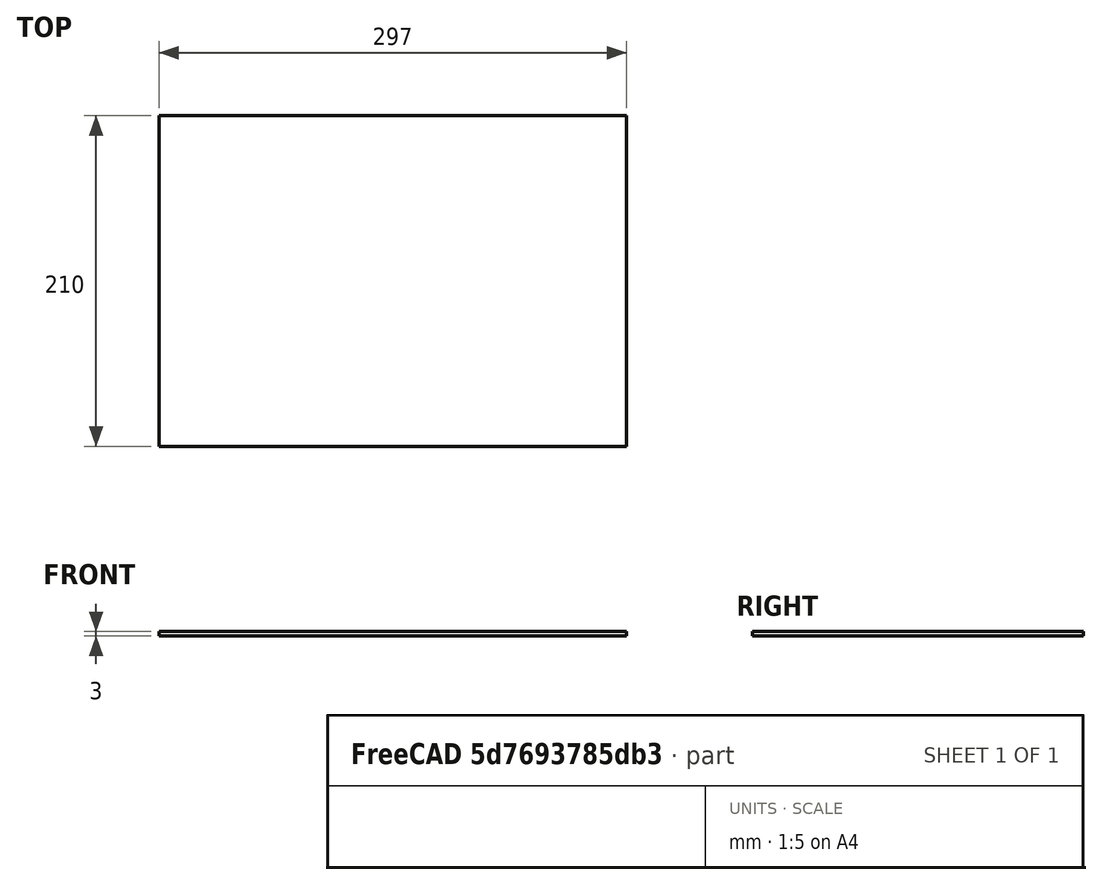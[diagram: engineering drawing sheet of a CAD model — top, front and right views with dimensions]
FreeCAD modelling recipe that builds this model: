
FCSTD DOCUMENT  (FreeCAD 0.20R29177 (Git))
Label: 1001_keyboard_Analog_wood_stencil_A4
License: All rights reserved
LicenseURL: http://en.wikipedia.org/wiki/All_rights_reserved
objects: Sketcher::SketchObject×3, PartDesign::Pad×1, PartDesign::Body×1
note: 6 computed .brp shape members not serialized (recipe doc carries the construction recipe); baked Part::Feature solids carry a one-line shape summary decoded from their .brp

FEATURE [Sketcher::SketchObject] Sketch
  FullyConstrained = true
  MapMode = 5
  Support = -> [XY_Plane]
  sketch-geometry (5):
    g0: LineSegment StartX=0 StartY=210 StartZ=0 EndX=297 EndY=210 EndZ=0
    g1: LineSegment StartX=297 StartY=210 StartZ=0 EndX=297 EndY=0 EndZ=0
    g2: LineSegment StartX=297 StartY=0 StartZ=0 EndX=0 EndY=0 EndZ=0
    g3: LineSegment StartX=0 StartY=0 StartZ=0 EndX=0 EndY=105 EndZ=0
    g4: LineSegment StartX=0 StartY=105 StartZ=0 EndX=0 EndY=210 EndZ=0
  constraints (14):
    c: Coincident(g0,g1)
    c: Coincident(g1,g2)
    c: Horizontal(g0)
    c: Horizontal(g2)
    c: Vertical(g1)
    c: DistanceY(g1,g1) = 210
    c: DistanceX(g0,g0) = 297
    c: Coincident(g3,g2)
    c: Coincident(g4,g0)
    c: Equal(g3,g4)
    c: Vertical(g4)
    c: Vertical(g3)
    c: Coincident(g3,g4)
    c: Coincident(g2,g-1)
FEATURE [PartDesign::Pad] Pad  label="A4_Landscape"
  AllowMultiFace = false
  Direction = (0,0,1)
  Length = 3
  Length2 = 100
  Profile = -> Sketch
  ReferenceAxis = -> Sketch [N_Axis]
  Type = 0
FEATURE [PartDesign::Body] Body
  Group = -> [Sketch,Pad]
  Origin = -> Origin
  Tip = -> Pad
FEATURE [Sketcher::SketchObject] Sketch003  label="JoystickLayout4Way"
  FullyConstrained = false
  sketch-geometry (78):
    g0: LineSegment StartX=34.7688 StartY=185.073 StartZ=0 EndX=129.769 EndY=185.073 EndZ=0
    g1: LineSegment StartX=129.769 StartY=185.073 StartZ=0 EndX=129.769 EndY=130.073 EndZ=0
    g2: LineSegment StartX=129.769 StartY=130.073 StartZ=0 EndX=82.2688 EndY=130.073 EndZ=0
    g3: LineSegment StartX=82.2688 StartY=130.073 StartZ=0 EndX=34.7688 EndY=130.073 EndZ=0
    g4: LineSegment StartX=34.7688 StartY=130.073 StartZ=0 EndX=34.7688 EndY=157.573 EndZ=0
    g5: LineSegment StartX=34.7688 StartY=157.573 StartZ=0 EndX=34.7688 EndY=185.073 EndZ=0
    g6: LineSegment StartX=34.7688 StartY=157.573 StartZ=0 EndX=82.2688 EndY=157.573 EndZ=0
    g7: Circle CenterX=82.2688 CenterY=157.573 CenterZ=0 NormalX=0 NormalY=0 NormalZ=1 AngleXU=0 Radius=15
    g8: LineSegment StartX=82.2688 StartY=157.573 StartZ=0 EndX=129.769 EndY=157.573 EndZ=0
    g9: ArcOfCircle CenterX=40.2688 CenterY=177.573 CenterZ=0 NormalX=0 NormalY=0 NormalZ=1 AngleXU=0 Radius=2.6 StartAngle=1.5708 EndAngle=4.71239
    g10: ArcOfCircle CenterX=42.8688 CenterY=177.573 CenterZ=0 NormalX=0 NormalY=0 NormalZ=1 AngleXU=0 Radius=2.6 StartAngle=4.71239 EndAngle=7.85398
    g11: LineSegment StartX=40.2688 StartY=174.973 StartZ=0 EndX=42.8688 EndY=174.973 EndZ=0
    g12: LineSegment StartX=42.8688 StartY=180.173 StartZ=0 EndX=40.2688 EndY=180.173 EndZ=0
    g13: LineSegment StartX=40.2688 StartY=180.173 StartZ=0 EndX=37.6688 EndY=180.173 EndZ=0
    g14: LineSegment StartX=42.8688 StartY=180.173 StartZ=0 EndX=45.4688 EndY=180.173 EndZ=0
    g15: ArcOfCircle CenterX=124.269 CenterY=177.573 CenterZ=0 NormalX=0 NormalY=0 NormalZ=1 AngleXU=0 Radius=2.6 StartAngle=4.71239 EndAngle=7.85398
    g16: LineSegment StartX=124.269 StartY=180.173 StartZ=0 EndX=121.669 EndY=180.173 EndZ=0
    g17: LineSegment StartX=121.669 StartY=174.973 StartZ=0 EndX=124.269 EndY=174.973 EndZ=0
    g18: ArcOfCircle CenterX=121.669 CenterY=177.573 CenterZ=0 NormalX=0 NormalY=0 NormalZ=1 AngleXU=0 Radius=2.6 StartAngle=1.5708 EndAngle=4.71239
    g19: LineSegment StartX=40.2688 StartY=134.973 StartZ=0 EndX=42.8688 EndY=134.973 EndZ=0
    g20: ArcOfCircle CenterX=42.8688 CenterY=137.573 CenterZ=0 NormalX=0 NormalY=0 NormalZ=1 AngleXU=0 Radius=2.6 StartAngle=4.71239 EndAngle=7.85398
    g21: LineSegment StartX=42.8688 StartY=140.173 StartZ=0 EndX=40.2688 EndY=140.173 EndZ=0
    g22: ArcOfCircle CenterX=40.2688 CenterY=137.573 CenterZ=0 NormalX=0 NormalY=0 NormalZ=1 AngleXU=0 Radius=2.6 StartAngle=1.5708 EndAngle=4.71239
    g23: ArcOfCircle CenterX=121.669 CenterY=137.573 CenterZ=0 NormalX=0 NormalY=0 NormalZ=1 AngleXU=0 Radius=2.6 StartAngle=1.5708 EndAngle=4.71239
    g24: LineSegment StartX=121.669 StartY=134.973 StartZ=0 EndX=124.269 EndY=134.973 EndZ=0
    g25: LineSegment StartX=124.269 StartY=140.173 StartZ=0 EndX=121.669 EndY=140.173 EndZ=0
    g26: ArcOfCircle CenterX=124.269 CenterY=137.573 CenterZ=0 NormalX=0 NormalY=0 NormalZ=1 AngleXU=0 Radius=2.6 StartAngle=4.71239 EndAngle=7.85398
    g27: LineSegment StartX=82.2688 StartY=130.073 StartZ=0 EndX=82.2688 EndY=132.973 EndZ=0
    g28: LineSegment StartX=34.7688 StartY=157.573 StartZ=0 EndX=37.6695 EndY=157.573 EndZ=0
    g29: LineSegment StartX=129.769 StartY=157.573 StartZ=0 EndX=126.868 EndY=157.573 EndZ=0
    g30: LineSegment StartX=82.2688 StartY=185.073 StartZ=0 EndX=82.2688 EndY=182.172 EndZ=0
    g31: LineSegment StartX=129.769 StartY=185.073 StartZ=0 EndX=72.7688 EndY=185.073 EndZ=0
    g32: LineSegment StartX=72.7688 StartY=185.073 StartZ=0 EndX=72.7688 EndY=195.073 EndZ=0
    g33: LineSegment StartX=52.7688 StartY=195.073 StartZ=0 EndX=52.7688 EndY=185.073 EndZ=0
    g34: LineSegment StartX=52.7688 StartY=185.073 StartZ=0 EndX=34.7688 EndY=185.073 EndZ=0
    g35: LineSegment StartX=52.7688 StartY=195.073 StartZ=0 EndX=62.7688 EndY=195.073 EndZ=0
    g36: LineSegment StartX=62.7688 StartY=195.073 StartZ=0 EndX=72.7688 EndY=195.073 EndZ=0
    g37: LineSegment StartX=40.2688 StartY=174.973 StartZ=0 EndX=40.2688 EndY=157.573 EndZ=0
    g38: LineSegment StartX=40.2688 StartY=157.573 StartZ=0 EndX=40.2688 EndY=140.173 EndZ=0
    g39: LineSegment StartX=33.7085 StartY=82.7474 StartZ=0 EndX=128.708 EndY=82.7474 EndZ=0
    g40: LineSegment StartX=128.708 StartY=82.7474 StartZ=0 EndX=128.708 EndY=27.7474 EndZ=0
    g41: LineSegment StartX=128.708 StartY=27.7474 StartZ=0 EndX=81.2085 EndY=27.7474 EndZ=0
    g42: LineSegment StartX=81.2085 StartY=27.7474 StartZ=0 EndX=33.7085 EndY=27.7474 EndZ=0
    g43: LineSegment StartX=33.7085 StartY=27.7474 StartZ=0 EndX=33.7085 EndY=55.2474 EndZ=0
    g44: LineSegment StartX=33.7085 StartY=55.2474 StartZ=0 EndX=33.7085 EndY=82.7474 EndZ=0
    g45: LineSegment StartX=33.7085 StartY=55.2474 StartZ=0 EndX=81.2085 EndY=55.2474 EndZ=0
    g46: Circle CenterX=81.2085 CenterY=55.2474 CenterZ=0 NormalX=0 NormalY=0 NormalZ=1 AngleXU=0 Radius=15
    g47: LineSegment StartX=81.2085 StartY=55.2474 StartZ=0 EndX=128.708 EndY=55.2474 EndZ=0
    g48: ArcOfCircle CenterX=39.2085 CenterY=75.2474 CenterZ=0 NormalX=0 NormalY=0 NormalZ=1 AngleXU=0 Radius=2.6 StartAngle=1.5708 EndAngle=4.71239
    g49: ArcOfCircle CenterX=41.8085 CenterY=75.2474 CenterZ=0 NormalX=0 NormalY=0 NormalZ=1 AngleXU=0 Radius=2.6 StartAngle=4.71239 EndAngle=7.85398
    g50: LineSegment StartX=39.2085 StartY=72.6474 StartZ=0 EndX=41.8085 EndY=72.6474 EndZ=0
    g51: LineSegment StartX=41.8085 StartY=77.8474 StartZ=0 EndX=39.2085 EndY=77.8474 EndZ=0
    g52: LineSegment StartX=39.2085 StartY=77.8474 StartZ=0 EndX=36.6085 EndY=77.8474 EndZ=0
    g53: LineSegment StartX=41.8085 StartY=77.8474 StartZ=0 EndX=44.4085 EndY=77.8474 EndZ=0
    g54: ArcOfCircle CenterX=123.208 CenterY=75.2474 CenterZ=0 NormalX=0 NormalY=0 NormalZ=1 AngleXU=0 Radius=2.6 StartAngle=4.71239 EndAngle=7.85398
    g55: LineSegment StartX=123.208 StartY=77.8474 StartZ=0 EndX=120.608 EndY=77.8474 EndZ=0
    g56: LineSegment StartX=120.608 StartY=72.6474 StartZ=0 EndX=123.208 EndY=72.6474 EndZ=0
    g57: ArcOfCircle CenterX=120.608 CenterY=75.2474 CenterZ=0 NormalX=0 NormalY=0 NormalZ=1 AngleXU=0 Radius=2.6 StartAngle=1.5708 EndAngle=4.71239
    g58: LineSegment StartX=39.2085 StartY=32.6474 StartZ=0 EndX=41.8085 EndY=32.6474 EndZ=0
    g59: ArcOfCircle CenterX=41.8085 CenterY=35.2474 CenterZ=0 NormalX=0 NormalY=0 NormalZ=1 AngleXU=0 Radius=2.6 StartAngle=4.71239 EndAngle=7.85398
    g60: LineSegment StartX=41.8085 StartY=37.8474 StartZ=0 EndX=39.2085 EndY=37.8474 EndZ=0
    g61: ArcOfCircle CenterX=39.2085 CenterY=35.2474 CenterZ=0 NormalX=0 NormalY=0 NormalZ=1 AngleXU=0 Radius=2.6 StartAngle=1.5708 EndAngle=4.71239
    g62: ArcOfCircle CenterX=120.608 CenterY=35.2474 CenterZ=0 NormalX=0 NormalY=0 NormalZ=1 AngleXU=0 Radius=2.6 StartAngle=1.5708 EndAngle=4.71239
    g63: LineSegment StartX=120.608 StartY=32.6474 StartZ=0 EndX=123.208 EndY=32.6474 EndZ=0
    g64: LineSegment StartX=123.208 StartY=37.8474 StartZ=0 EndX=120.608 EndY=37.8474 EndZ=0
    g65: ArcOfCircle CenterX=123.208 CenterY=35.2474 CenterZ=0 NormalX=0 NormalY=0 NormalZ=1 AngleXU=0 Radius=2.6 StartAngle=4.71239 EndAngle=7.85398
    g66: LineSegment StartX=81.2085 StartY=27.7474 StartZ=0 EndX=81.2085 EndY=30.6481 EndZ=0
    g67: LineSegment StartX=33.7085 StartY=55.2474 StartZ=0 EndX=36.6092 EndY=55.2474 EndZ=0
    g68: LineSegment StartX=128.708 StartY=55.2474 StartZ=0 EndX=125.808 EndY=55.2474 EndZ=0
    g69: LineSegment StartX=81.2085 StartY=82.7474 StartZ=0 EndX=81.2085 EndY=79.8467 EndZ=0
    g70: LineSegment StartX=128.708 StartY=82.7474 StartZ=0 EndX=71.7085 EndY=82.7474 EndZ=0
    g71: LineSegment StartX=71.7085 StartY=82.7474 StartZ=0 EndX=71.7085 EndY=92.7474 EndZ=0
    g72: LineSegment StartX=51.7085 StartY=92.7474 StartZ=0 EndX=51.7085 EndY=82.7474 EndZ=0
    g73: LineSegment StartX=51.7085 StartY=82.7474 StartZ=0 EndX=33.7085 EndY=82.7474 EndZ=0
    g74: LineSegment StartX=51.7085 StartY=92.7474 StartZ=0 EndX=61.7085 EndY=92.7474 EndZ=0
    g75: LineSegment StartX=61.7085 StartY=92.7474 StartZ=0 EndX=71.7085 EndY=92.7474 EndZ=0
    g76: LineSegment StartX=39.2085 StartY=72.6474 StartZ=0 EndX=39.2085 EndY=55.2474 EndZ=0
    g77: LineSegment StartX=39.2085 StartY=55.2474 StartZ=0 EndX=39.2085 EndY=37.8474 EndZ=0
  constraints (210):
    c: Coincident(g0,g1)
    c: Coincident(g1,g2)
    c: Horizontal(g0)
    c: Horizontal(g2)
    c: Vertical(g1)
    c: DistanceY(g1,g1) = 55
    c: DistanceX(g0,g0) = 95
    c: Coincident(g3,g2)
    c: Coincident(g4,g3)
    c: Coincident(g5,g4)
    c: Coincident(g5,g0)
    c: Vertical(g5)
    c: Vertical(g4)
    c: Horizontal(g3)
    c: Equal(g3,g2)
    c: Equal(g4,g5)
    c: Coincident(g6,g4)
    c: Horizontal(g6)
    c: Coincident(g7,g6)
    c: Coincident(g8,g6)
    c: PointOnObject(g8,g1)
    c: Horizontal(g8)
    c: Equal(g8,g6)
    c: Diameter(g7) = 30
    c: Tangent(g9,g11) = -1.5708
    c: Tangent(g11,g10) = -1.5708
    c: Tangent(g10,g12) = -1.5708
    c: Tangent(g12,g9) = -1.5708
    c: Equal(g9,g10)
    c: Horizontal(g11)
    c: DistanceY(g10,g10) = 5.2
    c: Coincident(g13,g9)
    c: Horizontal(g13)
    c: Coincident(g14,g10)
    c: Horizontal(g14)
    c: Equal(g14,g13)
    c: DistanceX(g13,g13) = 2.6
    c: DistanceX(g13,g14) = 7.8
    c: Tangent(g18,g17) = -1.5708
    c: Tangent(g17,g15) = -1.5708
    c: Tangent(g15,g16) = -1.5708
    c: Tangent(g16,g18) = -1.5708
    c: Equal(g18,g15)
    c: Horizontal(g17)
    c: Equal(g10,g15) = 5.2
    c: Tangent(g22,g19) = -1.5708
    c: Tangent(g19,g20) = -1.5708
    c: Tangent(g20,g21) = -1.5708
    c: Tangent(g21,g22) = -1.5708
    c: Equal(g22,g20)
    c: Horizontal(g19)
    c: Equal(g10,g20) = 5.2
    c: Tangent(g23,g24) = -1.5708
    c: Tangent(g24,g26) = -1.5708
    c: Tangent(g26,g25) = -1.5708
    c: Tangent(g25,g23) = -1.5708
    c: Equal(g23,g26)
    c: Horizontal(g24)
    c: Equal(g10,g26) = 5.2
    c: Equal(g21,g16)
    c: Equal(g16,g25)
    c: Equal(g25,g11)
    c: Vertical(g21,g9)
    c: DistanceX(g9,g6) = 42
    c: Horizontal(g23,g20)
    c: Vertical(g23,g17)
    c: DistanceX(g9,g15) = 84
    c: Horizontal(g10,g16)
    c: Coincident(g27,g2)
    c: Vertical(g27)
    c: Coincident(g28,g4)
    c: PointOnObject(g28,g6)
    c: Equal(g28,g27)
    c: Coincident(g29,g8)
    c: PointOnObject(g29,g8)
    c: Equal(g29,g27)
    c: PointOnObject(g30,g0)
    c: Vertical(g30)
    c: Equal(g30,g29)
    c: Vertical(g30,g27)
    c: Coincident(g31,g1)
    c: PointOnObject(g31,g0)
    c: Coincident(g32,g31)
    c: Vertical(g32)
    c: PointOnObject(g33,g0)
    c: Vertical(g33)
    c: Coincident(g34,g33)
    c: Coincident(g34,g5)
    c: DistanceX(g33,g32) = 20
    c: DistanceY(g33,g33) = 10
    c: Coincident(g35,g33)
    c: Horizontal(g35)
    c: Coincident(g36,g35)
    c: Coincident(g36,g32)
    c: Horizontal(g36)
    c: Equal(g36,g35)
    c: DistanceX(g5,g35) = 28
    c: Coincident(g37,g9)
    c: PointOnObject(g37,g6)
    c: Vertical(g37)
    c: Coincident(g38,g37)
    c: Coincident(g38,g21)
    c: Equal(g38,g37)
    c: DistanceY(g22,g9) = 40
    c: DistanceX(g7,g15) = 42
    c: Coincident(g39,g40)
    c: Coincident(g40,g41)
    c: Horizontal(g39)
    c: Horizontal(g41)
    c: Vertical(g40)
    c: DistanceY(g40,g40) = 55
    c: DistanceX(g39,g39) = 95
    c: Coincident(g42,g41)
    c: Coincident(g43,g42)
    c: Coincident(g44,g43)
    c: Coincident(g44,g39)
    c: Vertical(g44)
    c: Vertical(g43)
    c: Horizontal(g42)
    c: Equal(g42,g41)
    c: Equal(g43,g44)
    c: Coincident(g45,g43)
    c: Horizontal(g45)
    c: Coincident(g46,g45)
    c: Coincident(g47,g45)
    c: PointOnObject(g47,g40)
    c: Horizontal(g47)
    c: Equal(g47,g45)
    c: Diameter(g46) = 30
    c: Tangent(g48,g50) = -1.5708
    c: Tangent(g50,g49) = -1.5708
    c: Tangent(g49,g51) = -1.5708
    c: Tangent(g51,g48) = -1.5708
    c: Equal(g48,g49)
    c: Horizontal(g50)
    c: DistanceY(g49,g49) = 5.2
    c: Coincident(g52,g48)
    c: Horizontal(g52)
    c: Coincident(g53,g49)
    c: Horizontal(g53)
    c: Equal(g53,g52)
    c: DistanceX(g52,g52) = 2.6
    c: DistanceX(g52,g53) = 7.8
    c: Tangent(g57,g56) = -1.5708
    c: Tangent(g56,g54) = -1.5708
    c: Tangent(g54,g55) = -1.5708
    c: Tangent(g55,g57) = -1.5708
    c: Equal(g57,g54)
    c: Horizontal(g56)
    c: Equal(g49,g54) = 5.2
    c: Tangent(g61,g58) = -1.5708
    c: Tangent(g58,g59) = -1.5708
    c: Tangent(g59,g60) = -1.5708
    c: Tangent(g60,g61) = -1.5708
    c: Equal(g61,g59)
    c: Horizontal(g58)
    c: Equal(g49,g59) = 5.2
    c: Tangent(g62,g63) = -1.5708
    c: Tangent(g63,g65) = -1.5708
    c: Tangent(g65,g64) = -1.5708
    c: Tangent(g64,g62) = -1.5708
    c: Equal(g62,g65)
    c: Horizontal(g63)
    c: Equal(g49,g65) = 5.2
    c: Equal(g60,g55)
    c: Equal(g55,g64)
    c: Equal(g64,g50)
    c: Vertical(g60,g48)
    c: DistanceX(g48,g45) = 42
    c: Horizontal(g62,g59)
    c: Vertical(g62,g56)
    c: DistanceX(g48,g54) = 84
    c: Horizontal(g49,g55)
    c: Coincident(g66,g41)
    c: Vertical(g66)
    c: Coincident(g67,g43)
    c: PointOnObject(g67,g45)
    c: Equal(g67,g66)
    c: Coincident(g68,g47)
    c: PointOnObject(g68,g47)
    c: Equal(g68,g66)
    c: PointOnObject(g69,g39)
    c: Vertical(g69)
    c: Equal(g69,g68)
    c: Vertical(g69,g66)
    c: Coincident(g70,g40)
    c: PointOnObject(g70,g39)
    c: Coincident(g71,g70)
    c: Vertical(g71)
    c: PointOnObject(g72,g39)
    c: Vertical(g72)
    c: Coincident(g73,g72)
    c: Coincident(g73,g44)
    c: DistanceX(g72,g71) = 20
    c: DistanceY(g72,g72) = 10
    c: Coincident(g74,g72)
    c: Horizontal(g74)
    c: Coincident(g75,g74)
    c: Coincident(g75,g71)
    c: Horizontal(g75)
    c: Equal(g75,g74)
    c: DistanceX(g44,g74) = 28
    c: Coincident(g76,g48)
    c: PointOnObject(g76,g45)
    c: Vertical(g76)
    c: Coincident(g77,g76)
    c: Coincident(g77,g60)
    c: Equal(g77,g76)
    c: DistanceY(g61,g48) = 40
    c: DistanceX(g46,g54) = 42
FEATURE [Sketcher::SketchObject] Sketch007  label="JoystickAnalog"
  FullyConstrained = false
  MapMode = 5
  Support = -> [XY_Plane]
  sketch-geometry (90):
    g0: Circle CenterX=230.411 CenterY=57.5212 CenterZ=0 NormalX=0 NormalY=0 NormalZ=1 AngleXU=0 Radius=20
    g1: LineSegment StartX=230.411 StartY=57.5212 StartZ=0 EndX=187.911 EndY=57.5212 EndZ=0
    g2: LineSegment StartX=230.411 StartY=57.5212 StartZ=0 EndX=272.911 EndY=57.5212 EndZ=0
    g3: LineSegment StartX=187.911 StartY=57.5212 StartZ=0 EndX=187.911 EndY=77.5212 EndZ=0
    g4: LineSegment StartX=187.911 StartY=57.5212 StartZ=0 EndX=187.911 EndY=37.5212 EndZ=0
    g5: LineSegment StartX=272.911 StartY=57.5212 StartZ=0 EndX=272.911 EndY=37.5212 EndZ=0
    g6: LineSegment StartX=272.911 StartY=57.5212 StartZ=0 EndX=272.911 EndY=77.5212 EndZ=0
    g7: LineSegment StartX=230.411 StartY=57.5212 StartZ=0 EndX=230.411 EndY=87.5212 EndZ=0
    g8: LineSegment StartX=230.411 StartY=57.5212 StartZ=0 EndX=230.411 EndY=27.5212 EndZ=0
    g9: LineSegment StartX=230.411 StartY=87.5212 StartZ=0 EndX=182.911 EndY=87.5212 EndZ=0
    g10: LineSegment StartX=230.411 StartY=87.5212 StartZ=0 EndX=277.911 EndY=87.5212 EndZ=0
    g11: LineSegment StartX=230.411 StartY=27.5212 StartZ=0 EndX=182.911 EndY=27.5212 EndZ=0
    g12: LineSegment StartX=182.911 StartY=27.5212 StartZ=0 EndX=182.911 EndY=87.5212 EndZ=0
    g13: LineSegment StartX=230.411 StartY=27.5212 StartZ=0 EndX=277.911 EndY=27.5212 EndZ=0
    g14: LineSegment StartX=277.911 StartY=27.5212 StartZ=0 EndX=277.911 EndY=87.5212 EndZ=0
    g15: ArcOfCircle CenterX=187.911 CenterY=77.5212 CenterZ=0 NormalX=0 NormalY=0 NormalZ=1 AngleXU=0 Radius=2.5 StartAngle=1.5708 EndAngle=4.71239
    g16: ArcOfCircle CenterX=192.911 CenterY=77.5212 CenterZ=0 NormalX=0 NormalY=0 NormalZ=1 AngleXU=0 Radius=2.5 StartAngle=4.71239 EndAngle=7.85398
    g17: LineSegment StartX=187.911 StartY=75.0212 StartZ=0 EndX=192.911 EndY=75.0212 EndZ=0
    g18: LineSegment StartX=192.911 StartY=80.0212 StartZ=0 EndX=187.911 EndY=80.0212 EndZ=0
    g19: ArcOfCircle CenterX=187.911 CenterY=37.5212 CenterZ=0 NormalX=0 NormalY=0 NormalZ=1 AngleXU=0 Radius=2.5 StartAngle=1.5708 EndAngle=4.71239
    g20: ArcOfCircle CenterX=192.911 CenterY=37.5212 CenterZ=0 NormalX=0 NormalY=0 NormalZ=1 AngleXU=0 Radius=2.5 StartAngle=4.71239 EndAngle=7.85398
    g21: LineSegment StartX=187.911 StartY=35.0212 StartZ=0 EndX=192.911 EndY=35.0212 EndZ=0
    g22: LineSegment StartX=192.911 StartY=40.0212 StartZ=0 EndX=187.911 EndY=40.0212 EndZ=0
    g23: ArcOfCircle CenterX=272.911 CenterY=37.5212 CenterZ=0 NormalX=0 NormalY=0 NormalZ=1 AngleXU=0 Radius=2.5 StartAngle=4.71239 EndAngle=7.85398
    g24: ArcOfCircle CenterX=267.911 CenterY=37.5212 CenterZ=0 NormalX=0 NormalY=0 NormalZ=1 AngleXU=0 Radius=2.5 StartAngle=1.5708 EndAngle=4.71239
    g25: LineSegment StartX=272.911 StartY=40.0212 StartZ=0 EndX=267.911 EndY=40.0212 EndZ=0
    g26: LineSegment StartX=267.911 StartY=35.0212 StartZ=0 EndX=272.911 EndY=35.0212 EndZ=0
    g27: ArcOfCircle CenterX=272.911 CenterY=77.5212 CenterZ=0 NormalX=0 NormalY=0 NormalZ=1 AngleXU=0 Radius=2.5 StartAngle=4.71239 EndAngle=7.85398
    g28: ArcOfCircle CenterX=267.911 CenterY=77.5212 CenterZ=0 NormalX=0 NormalY=0 NormalZ=1 AngleXU=0 Radius=2.5 StartAngle=1.5708 EndAngle=4.71239
    g29: LineSegment StartX=272.911 StartY=80.0212 StartZ=0 EndX=267.911 EndY=80.0212 EndZ=0
    g30: LineSegment StartX=267.911 StartY=75.0212 StartZ=0 EndX=272.911 EndY=75.0212 EndZ=0
    g31: LineSegment StartX=187.911 StartY=57.5212 StartZ=0 EndX=182.911 EndY=57.5212 EndZ=0
    g32: LineSegment StartX=272.911 StartY=57.5212 StartZ=0 EndX=277.911 EndY=57.5212 EndZ=0
    g33: LineSegment StartX=230.411 StartY=87.5212 StartZ=0 EndX=230.411 EndY=82.5212 EndZ=0
    g34: LineSegment StartX=182.911 StartY=27.5212 StartZ=0 EndX=222.911 EndY=27.5212 EndZ=0
    g35: LineSegment StartX=222.911 StartY=27.5212 StartZ=0 EndX=222.911 EndY=15.5212 EndZ=0
    g36: LineSegment StartX=222.911 StartY=15.5212 StartZ=0 EndX=237.911 EndY=15.5212 EndZ=0
    g37: LineSegment StartX=237.911 StartY=15.5212 StartZ=0 EndX=237.911 EndY=27.5212 EndZ=0
    g38: LineSegment StartX=237.911 StartY=27.5212 StartZ=0 EndX=277.911 EndY=27.5212 EndZ=0
    g39: LineSegment StartX=182.911 StartY=87.5212 StartZ=0 EndX=215.411 EndY=87.5212 EndZ=0
    g40: LineSegment StartX=215.411 StartY=87.5212 StartZ=0 EndX=215.411 EndY=91.5212 EndZ=0
    g41: LineSegment StartX=220.411 StartY=91.5212 StartZ=0 EndX=220.411 EndY=87.5212 EndZ=0
    g42: LineSegment StartX=220.411 StartY=87.5212 StartZ=0 EndX=230.411 EndY=87.5212 EndZ=0
    g43: LineSegment StartX=215.411 StartY=91.5212 StartZ=0 EndX=217.911 EndY=91.5212 EndZ=0
    g44: LineSegment StartX=217.911 StartY=91.5212 StartZ=0 EndX=220.411 EndY=91.5212 EndZ=0
    g45: Circle CenterX=228.24 CenterY=157.793 CenterZ=0 NormalX=0 NormalY=0 NormalZ=1 AngleXU=0 Radius=20
    g46: LineSegment StartX=228.24 StartY=157.793 StartZ=0 EndX=185.74 EndY=157.793 EndZ=0
    g47: LineSegment StartX=228.24 StartY=157.793 StartZ=0 EndX=270.74 EndY=157.793 EndZ=0
    g48: LineSegment StartX=185.74 StartY=157.793 StartZ=0 EndX=185.74 EndY=177.793 EndZ=0
    g49: LineSegment StartX=185.74 StartY=157.793 StartZ=0 EndX=185.74 EndY=137.793 EndZ=0
    g50: LineSegment StartX=270.74 StartY=157.793 StartZ=0 EndX=270.74 EndY=137.793 EndZ=0
    g51: LineSegment StartX=270.74 StartY=157.793 StartZ=0 EndX=270.74 EndY=177.793 EndZ=0
    g52: LineSegment StartX=228.24 StartY=157.793 StartZ=0 EndX=228.24 EndY=187.793 EndZ=0
    g53: LineSegment StartX=228.24 StartY=157.793 StartZ=0 EndX=228.24 EndY=127.793 EndZ=0
    g54: LineSegment StartX=228.24 StartY=187.793 StartZ=0 EndX=180.74 EndY=187.793 EndZ=0
    g55: LineSegment StartX=228.24 StartY=187.793 StartZ=0 EndX=275.74 EndY=187.793 EndZ=0
    g56: LineSegment StartX=228.24 StartY=127.793 StartZ=0 EndX=180.74 EndY=127.793 EndZ=0
    g57: LineSegment StartX=180.74 StartY=127.793 StartZ=0 EndX=180.74 EndY=187.793 EndZ=0
    g58: LineSegment StartX=228.24 StartY=127.793 StartZ=0 EndX=275.74 EndY=127.793 EndZ=0
    g59: LineSegment StartX=275.74 StartY=127.793 StartZ=0 EndX=275.74 EndY=187.793 EndZ=0
    g60: ArcOfCircle CenterX=185.74 CenterY=177.793 CenterZ=0 NormalX=0 NormalY=0 NormalZ=1 AngleXU=0 Radius=2.5 StartAngle=1.5708 EndAngle=4.71239
    g61: ArcOfCircle CenterX=190.74 CenterY=177.793 CenterZ=0 NormalX=0 NormalY=0 NormalZ=1 AngleXU=0 Radius=2.5 StartAngle=4.71239 EndAngle=7.85398
    g62: LineSegment StartX=185.74 StartY=175.293 StartZ=0 EndX=190.74 EndY=175.293 EndZ=0
    g63: LineSegment StartX=190.74 StartY=180.293 StartZ=0 EndX=185.74 EndY=180.293 EndZ=0
    g64: ArcOfCircle CenterX=185.74 CenterY=137.793 CenterZ=0 NormalX=0 NormalY=0 NormalZ=1 AngleXU=0 Radius=2.5 StartAngle=1.5708 EndAngle=4.71239
    g65: ArcOfCircle CenterX=190.74 CenterY=137.793 CenterZ=0 NormalX=0 NormalY=0 NormalZ=1 AngleXU=0 Radius=2.5 StartAngle=4.71239 EndAngle=7.85398
    g66: LineSegment StartX=185.74 StartY=135.293 StartZ=0 EndX=190.74 EndY=135.293 EndZ=0
    g67: LineSegment StartX=190.74 StartY=140.293 StartZ=0 EndX=185.74 EndY=140.293 EndZ=0
    g68: ArcOfCircle CenterX=270.74 CenterY=137.793 CenterZ=0 NormalX=0 NormalY=0 NormalZ=1 AngleXU=0 Radius=2.5 StartAngle=4.71239 EndAngle=7.85398
    g69: ArcOfCircle CenterX=265.74 CenterY=137.793 CenterZ=0 NormalX=0 NormalY=0 NormalZ=1 AngleXU=0 Radius=2.5 StartAngle=1.5708 EndAngle=4.71239
    g70: LineSegment StartX=270.74 StartY=140.293 StartZ=0 EndX=265.74 EndY=140.293 EndZ=0
    g71: LineSegment StartX=265.74 StartY=135.293 StartZ=0 EndX=270.74 EndY=135.293 EndZ=0
    g72: ArcOfCircle CenterX=270.74 CenterY=177.793 CenterZ=0 NormalX=0 NormalY=0 NormalZ=1 AngleXU=0 Radius=2.5 StartAngle=4.71239 EndAngle=7.85398
    g73: ArcOfCircle CenterX=265.74 CenterY=177.793 CenterZ=0 NormalX=0 NormalY=0 NormalZ=1 AngleXU=0 Radius=2.5 StartAngle=1.5708 EndAngle=4.71239
    g74: LineSegment StartX=270.74 StartY=180.293 StartZ=0 EndX=265.74 EndY=180.293 EndZ=0
    g75: LineSegment StartX=265.74 StartY=175.293 StartZ=0 EndX=270.74 EndY=175.293 EndZ=0
    g76: LineSegment StartX=185.74 StartY=157.793 StartZ=0 EndX=180.74 EndY=157.793 EndZ=0
    g77: LineSegment StartX=270.74 StartY=157.793 StartZ=0 EndX=275.74 EndY=157.793 EndZ=0
    g78: LineSegment StartX=228.24 StartY=187.793 StartZ=0 EndX=228.24 EndY=182.793 EndZ=0
    g79: LineSegment StartX=180.74 StartY=127.793 StartZ=0 EndX=220.74 EndY=127.793 EndZ=0
    g80: LineSegment StartX=220.74 StartY=127.793 StartZ=0 EndX=220.74 EndY=115.793 EndZ=0
    g81: LineSegment StartX=220.74 StartY=115.793 StartZ=0 EndX=235.74 EndY=115.793 EndZ=0
    g82: LineSegment StartX=235.74 StartY=115.793 StartZ=0 EndX=235.74 EndY=127.793 EndZ=0
    g83: LineSegment StartX=235.74 StartY=127.793 StartZ=0 EndX=275.74 EndY=127.793 EndZ=0
    g84: LineSegment StartX=180.74 StartY=187.793 StartZ=0 EndX=213.24 EndY=187.793 EndZ=0
    g85: LineSegment StartX=213.24 StartY=187.793 StartZ=0 EndX=213.24 EndY=191.793 EndZ=0
    g86: LineSegment StartX=218.24 StartY=191.793 StartZ=0 EndX=218.24 EndY=187.793 EndZ=0
    g87: LineSegment StartX=218.24 StartY=187.793 StartZ=0 EndX=228.24 EndY=187.793 EndZ=0
    g88: LineSegment StartX=213.24 StartY=191.793 StartZ=0 EndX=215.74 EndY=191.793 EndZ=0
    g89: LineSegment StartX=215.74 StartY=191.793 StartZ=0 EndX=218.24 EndY=191.793 EndZ=0
  constraints (234):
    c: Diameter(g0) = 40
    c: Coincident(g1,g0)
    c: Horizontal(g1)
    c: Coincident(g2,g0)
    c: Horizontal(g2)
    c: Coincident(g3,g1)
    c: Vertical(g3)
    c: Coincident(g4,g1)
    c: Vertical(g4)
    c: Coincident(g5,g2)
    c: Vertical(g5)
    c: Coincident(g6,g2)
    c: Vertical(g6)
    c: Equal(g4,g3)
    c: Equal(g3,g5)
    c: Equal(g5,g6)
    c: Equal(g2,g1)
    c: Coincident(g7,g0)
    c: Vertical(g7)
    c: Coincident(g8,g0)
    c: Vertical(g8)
    c: Equal(g8,g7)
    c: DistanceY(g4,g3) = 40
    c: DistanceX(g3,g6) = 85
    c: DistanceY(g8,g7) = 60
    c: Coincident(g9,g7)
    c: Coincident(g10,g9)
    c: Equal(g10,g9)
    c: Horizontal(g9)
    c: Horizontal(g10)
    c: DistanceX(g9,g10) = 95
    c: Coincident(g11,g8)
    c: Horizontal(g11)
    c: Coincident(g12,g9)
    c: Vertical(g12)
    c: Coincident(g13,g11)
    c: Coincident(g14,g13)
    c: Coincident(g14,g10)
    c: Horizontal(g13)
    c: Vertical(g14)
    c: Coincident(g11,g12)
    c: Tangent(g15,g17) = -1.5708
    c: Tangent(g17,g16) = -1.5708
    c: Tangent(g16,g18) = -1.5708
    c: Tangent(g18,g15) = -1.5708
    c: Equal(g15,g16)
    c: Coincident(g15,g3)
    c: Horizontal(g17)
    c: Tangent(g19,g21) = -1.5708
    c: Tangent(g21,g20) = -1.5708
    c: Tangent(g20,g22) = -1.5708
    c: Tangent(g22,g19) = -1.5708
    c: Equal(g19,g20)
    c: Coincident(g19,g4)
    c: Horizontal(g21)
    c: Tangent(g23,g25) = -1.5708
    c: Tangent(g25,g24) = -1.5708
    c: Tangent(g24,g26) = -1.5708
    c: Tangent(g26,g23) = -1.5708
    c: Equal(g23,g24)
    c: Coincident(g23,g5)
    c: Horizontal(g25)
    c: Tangent(g27,g29) = -1.5708
    c: Tangent(g29,g28) = -1.5708
    c: Tangent(g28,g30) = -1.5708
    c: Tangent(g30,g27) = -1.5708
    c: Equal(g27,g28)
    c: Coincident(g27,g6)
    c: Horizontal(g29)
    c: Equal(g18,g22)
    c: Equal(g22,g25)
    c: Equal(g25,g29)
    c: Equal(g20,g24)
    c: Equal(g24,g28)
    c: Equal(g28,g16)
    c: Diameter(g16) = 5
    c: DistanceX(g18,g18) = 5
    c: Coincident(g31,g1)
    c: PointOnObject(g31,g12)
    c: Horizontal(g31)
    c: Coincident(g32,g2)
    c: PointOnObject(g32,g14)
    c: Horizontal(g32)
    c: Coincident(g33,g9)
    c: PointOnObject(g33,g7)
    c: Equal(g33,g32)
    c: Coincident(g34,g12)
    c: PointOnObject(g34,g11)
    c: Coincident(g35,g34)
    c: Vertical(g35)
    c: Coincident(g36,g35)
    c: Horizontal(g36)
    c: Coincident(g37,g36)
    c: PointOnObject(g37,g13)
    c: Coincident(g38,g37)
    c: Coincident(g38,g14)
    c: Equal(g38,g34)
    c: DistanceX(g36,g36) = 15
    c: DistanceY(g35,g35) = 12
    c: Coincident(g39,g12)
    c: PointOnObject(g39,g9)
    c: Coincident(g40,g39)
    c: PointOnObject(g41,g9)
    c: Coincident(g42,g41)
    c: Coincident(g42,g10)
    c: Vertical(g40)
    c: Vertical(g41)
    c: Coincident(g43,g40)
    c: Horizontal(g43)
    c: Coincident(g44,g43)
    c: Coincident(g44,g41)
    c: Horizontal(g44)
    c: Equal(g44,g43)
    c: DistanceX(g12,g43) = 35
    c: DistanceX(g40,g41) = 5
    c: DistanceY(g40,g40) = 4
    c: Vertical(g37)
    c: Equal(g0,g45) = 40
    c: Coincident(g46,g45)
    c: Horizontal(g46)
    c: Coincident(g47,g45)
    c: Horizontal(g47)
    c: Coincident(g48,g46)
    c: Vertical(g48)
    c: Coincident(g49,g46)
    c: Vertical(g49)
    c: Coincident(g50,g47)
    c: Vertical(g50)
    c: Coincident(g51,g47)
    c: Vertical(g51)
    c: Equal(g49,g48)
    c: Equal(g48,g50)
    c: Equal(g50,g51)
    c: Equal(g47,g46)
    c: Coincident(g52,g45)
    c: Vertical(g52)
    c: Coincident(g53,g45)
    c: Vertical(g53)
    c: Equal(g53,g52)
    c: DistanceY(g49,g48) = 40
    c: DistanceX(g48,g51) = 85
    c: DistanceY(g53,g52) = 60
    c: Coincident(g54,g52)
    c: Coincident(g55,g54)
    c: Equal(g55,g54)
    c: Horizontal(g54)
    c: Horizontal(g55)
    c: DistanceX(g54,g55) = 95
    c: Coincident(g56,g53)
    c: Horizontal(g56)
    c: Coincident(g57,g54)
    c: Vertical(g57)
    c: Coincident(g58,g56)
    c: Coincident(g59,g58)
    c: Coincident(g59,g55)
    c: Horizontal(g58)
    c: Vertical(g59)
    c: Coincident(g56,g57)
    c: Tangent(g60,g62) = -1.5708
    c: Tangent(g62,g61) = -1.5708
    c: Tangent(g61,g63) = -1.5708
    c: Tangent(g63,g60) = -1.5708
    c: Equal(g60,g61)
    c: Coincident(g60,g48)
    c: Horizontal(g62)
    c: Tangent(g64,g66) = -1.5708
    c: Tangent(g66,g65) = -1.5708
    c: Tangent(g65,g67) = -1.5708
    c: Tangent(g67,g64) = -1.5708
    c: Equal(g64,g65)
    c: Coincident(g64,g49)
    c: Horizontal(g66)
    c: Tangent(g68,g70) = -1.5708
    c: Tangent(g70,g69) = -1.5708
    c: Tangent(g69,g71) = -1.5708
    c: Tangent(g71,g68) = -1.5708
    c: Equal(g68,g69)
    c: Coincident(g68,g50)
    c: Horizontal(g70)
    c: Tangent(g72,g74) = -1.5708
    c: Tangent(g74,g73) = -1.5708
    c: Tangent(g73,g75) = -1.5708
    c: Tangent(g75,g72) = -1.5708
    c: Equal(g72,g73)
    c: Coincident(g72,g51)
    c: Horizontal(g74)
    c: Equal(g63,g67)
    c: Equal(g67,g70)
    c: Equal(g70,g74)
    c: Equal(g65,g69)
    c: Equal(g69,g73)
    c: Equal(g73,g61)
    c: Equal(g16,g61) = 5
    c: Equal(g18,g63) = 5
    c: Coincident(g76,g46)
    c: PointOnObject(g76,g57)
    c: Horizontal(g76)
    c: Coincident(g77,g47)
    c: PointOnObject(g77,g59)
    c: Horizontal(g77)
    c: Coincident(g78,g54)
    c: PointOnObject(g78,g52)
    c: Equal(g78,g77)
    c: Coincident(g79,g57)
    c: PointOnObject(g79,g56)
    c: Coincident(g80,g79)
    c: Vertical(g80)
    c: Coincident(g81,g80)
    c: Horizontal(g81)
    c: Coincident(g82,g81)
    c: PointOnObject(g82,g58)
    c: Coincident(g83,g82)
    c: Coincident(g83,g59)
    c: Equal(g83,g79)
    c: Equal(g36,g81) = 15
    c: Equal(g35,g80) = 12
    c: Coincident(g84,g57)
    c: PointOnObject(g84,g54)
    c: Coincident(g85,g84)
    c: PointOnObject(g86,g54)
    c: Coincident(g87,g86)
    c: Coincident(g87,g55)
    c: Vertical(g85)
    c: Vertical(g86)
    c: Coincident(g88,g85)
    c: Horizontal(g88)
    c: Coincident(g89,g88)
    c: Coincident(g89,g86)
    c: Horizontal(g89)
    c: Equal(g89,g88)
    c: DistanceX(g57,g88) = 35
    c: DistanceX(g85,g86) = 5
    c: Equal(g40,g85) = 4
    c: Vertical(g82)
